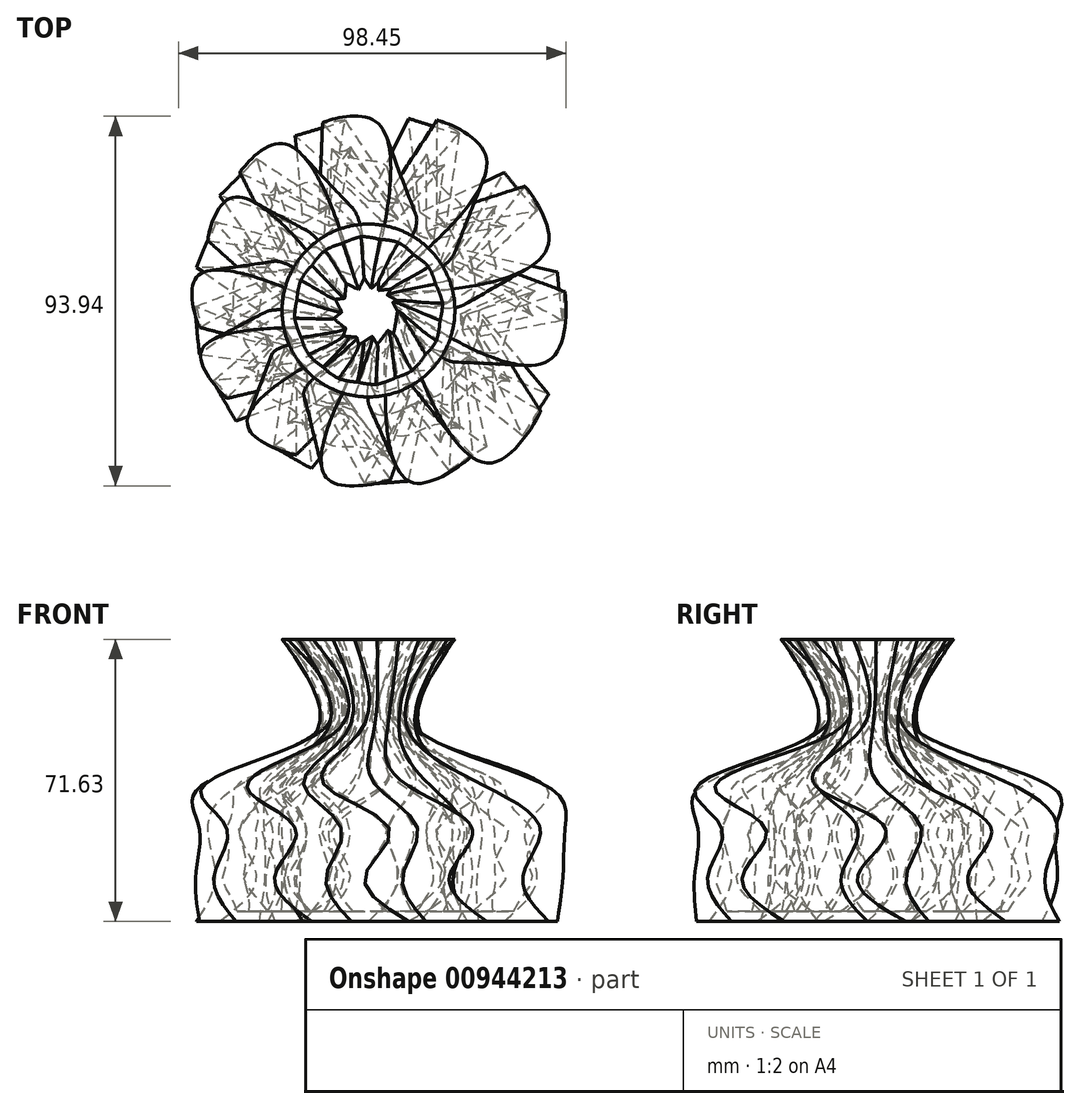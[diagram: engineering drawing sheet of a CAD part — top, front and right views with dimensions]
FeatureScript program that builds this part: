
annotation { "Feature Type Name" : "Feature", "Feature Type Description" : "" }
export const myFeature = defineFeature(function(context is Context, id is Id, definition is map)
    precondition{}
    {
        {
            var Q0;
            Q0=qCreatedBy(makeId("Top.planeOp"),FACE);
            var sketch = newSketch(context, id + "F0", { "sketchPlane" : qUnion([Q0])});
            skLineSegment(sketch, "E0", {"start": v(0, 27.93) * mm, "end": v(-18.62, 44.4) * mm});
            skLineSegment(sketch, "E1", {"start": v(-18.62, 44.4) * mm, "end": v(-16.65, 22.27) * mm});
            skLineSegment(sketch, "E2", {"start": v(-16.65, 22.27) * mm, "end": v(-37.8, 29.15) * mm});
            skLineSegment(sketch, "E3", {"start": v(-37.8, 29.15) * mm, "end": v(-25.5, 10.96) * mm});
            skLineSegment(sketch, "E4", {"start": v(-25.5, 10.96) * mm, "end": v(-43.7, 10.96) * mm});
            skLineSegment(sketch, "E5", {"start": v(-43.7, 10.96) * mm, "end": v(-27.71, 0) * mm});
            skLineSegment(sketch, "E6", {"start": v(-27.71, 0) * mm, "end": v(-42.95, -11.16) * mm});
            skLineSegment(sketch, "E7", {"start": v(-42.95, -11.16) * mm, "end": v(-23.78, -13.62) * mm});
            skLineSegment(sketch, "E8", {"start": v(-23.78, -13.62) * mm, "end": v(-33.61, -28.12) * mm});
            skLineSegment(sketch, "E9", {"start": v(-33.61, -28.12) * mm, "end": v(-16.65, -21.73) * mm});
            skLineSegment(sketch, "E10", {"start": v(-16.65, -21.73) * mm, "end": v(-14.44, -40.16) * mm});
            skLineSegment(sketch, "E11", {"start": v(-14.44, -40.16) * mm, "end": v(-4.36, -27.14) * mm});
            skLineSegment(sketch, "E12", {"start": v(-4.36, -27.14) * mm, "end": v(10.14, -43.36) * mm});
            skLineSegment(sketch, "E13", {"start": v(10.14, -43.36) * mm, "end": v(14.56, -22.71) * mm});
            skLineSegment(sketch, "E14", {"start": v(14.56, -22.71) * mm, "end": v(30.05, -34.5) * mm});
            skLineSegment(sketch, "E15", {"start": v(30.05, -34.5) * mm, "end": v(25.13, -12.39) * mm});
            skLineSegment(sketch, "E16", {"start": v(25.13, -12.39) * mm, "end": v(45.78, -21.24) * mm});
            skLineSegment(sketch, "E17", {"start": v(45.78, -21.24) * mm, "end": v(28.08, 0) * mm});
            skLineSegment(sketch, "E18", {"start": v(28.08, 0) * mm, "end": v(48, 9.74) * mm});
            skLineSegment(sketch, "E19", {"start": v(48, 9.74) * mm, "end": v(22.68, 15.64) * mm});
            skLineSegment(sketch, "E20", {"start": v(22.68, 15.64) * mm, "end": v(34.47, 35.05) * mm});
            skLineSegment(sketch, "E21", {"start": v(34.47, 35.05) * mm, "end": v(13.09, 24.98) * mm});
            skLineSegment(sketch, "E22", {"start": v(13.09, 24.98) * mm, "end": v(10.14, 48.82) * mm});
            skLineSegment(sketch, "E23", {"start": v(10.14, 48.82) * mm, "end": v(0, 27.93) * mm});
            skSolve(sketch);
        }
        {
            var Q0;
            Q0=qCreatedBy(makeId("Top.planeOp"),FACE);
            cPlane(context, id + "F1", {"entities" : qUnion([Q0]), "cplaneType" : CPlaneType.OFFSET, "offset" : 11.68 * mm, "width" : 152.4 * mm, "height" : 152.4 * mm});
        }
        {
            var Q0;
            Q0=qCreatedBy(makeId("Top.planeOp"),FACE);
            cPlane(context, id + "F2", {"entities" : qUnion([Q0]), "cplaneType" : CPlaneType.OFFSET, "offset" : 23.37 * mm, "width" : 152.4 * mm, "height" : 152.4 * mm});
        }
        {
            var Q0;
            Q0=qCreatedBy(makeId("Top.planeOp"),FACE);
            cPlane(context, id + "F3", {"entities" : qUnion([Q0]), "cplaneType" : CPlaneType.OFFSET, "offset" : 33.02 * mm, "width" : 152.4 * mm, "height" : 152.4 * mm});
        }
        {
            var Q0;
            Q0=qCreatedBy(makeId("Top.planeOp"),FACE);
            cPlane(context, id + "F4", {"entities" : qUnion([Q0]), "cplaneType" : CPlaneType.OFFSET, "offset" : 48 * mm, "width" : 152.4 * mm, "height" : 152.4 * mm});
        }
        {
            var Q0;
            Q0=qCreatedBy(makeId("Top.planeOp"),FACE);
            cPlane(context, id + "F5", {"entities" : qUnion([Q0]), "cplaneType" : CPlaneType.OFFSET, "offset" : 71.63 * mm, "width" : 152.4 * mm, "height" : 152.4 * mm});
        }
        {
            var Q0;
            Q0=qCreatedBy(id+"F1.planeOp",FACE);
            var sketch = newSketch(context, id + "F6", { "sketchPlane" : qUnion([Q0])});
            skLineSegment(sketch, "E24", {"start": v(7.76, 27.61) * mm, "end": v(-5.97, 48.34) * mm});
            skLineSegment(sketch, "E25", {"start": v(-5.97, 48.34) * mm, "end": v(-9.8, 26.46) * mm});
            skLineSegment(sketch, "E26", {"start": v(-9.8, 26.46) * mm, "end": v(-28.43, 38.58) * mm});
            skLineSegment(sketch, "E27", {"start": v(-28.43, 38.58) * mm, "end": v(-21.27, 17.83) * mm});
            skLineSegment(sketch, "E28", {"start": v(-21.27, 17.83) * mm, "end": v(-38.84, 22.54) * mm});
            skLineSegment(sketch, "E29", {"start": v(-38.84, 22.54) * mm, "end": v(-26.24, 7.81) * mm});
            skLineSegment(sketch, "E30", {"start": v(-26.24, 7.81) * mm, "end": v(-43.85, 0.98) * mm});
            skLineSegment(sketch, "E31", {"start": v(-43.85, 0.98) * mm, "end": v(-25.97, -6.36) * mm});
            skLineSegment(sketch, "E32", {"start": v(-25.97, -6.36) * mm, "end": v(-39.22, -17.82) * mm});
            skLineSegment(sketch, "E33", {"start": v(-39.22, -17.82) * mm, "end": v(-21.18, -16.04) * mm});
            skLineSegment(sketch, "E34", {"start": v(-21.18, -16.04) * mm, "end": v(-23.82, -34.42) * mm});
            skLineSegment(sketch, "E35", {"start": v(-23.82, -34.42) * mm, "end": v(-10.7, -24.44) * mm});
            skLineSegment(sketch, "E36", {"start": v(-10.7, -24.44) * mm, "end": v(-0.9, -43.87) * mm});
            skLineSegment(sketch, "E37", {"start": v(-0.9, -43.87) * mm, "end": v(8.72, -25.07) * mm});
            skLineSegment(sketch, "E38", {"start": v(8.72, -25.07) * mm, "end": v(20.62, -40.47) * mm});
            skLineSegment(sketch, "E39", {"start": v(20.62, -40.47) * mm, "end": v(21.6, -17.83) * mm});
            skLineSegment(sketch, "E40", {"start": v(21.6, -17.83) * mm, "end": v(39.25, -31.72) * mm});
            skLineSegment(sketch, "E41", {"start": v(39.25, -31.72) * mm, "end": v(27.66, -6.63) * mm});
            skLineSegment(sketch, "E42", {"start": v(27.66, -6.63) * mm, "end": v(49.4, -2.38) * mm});
            skLineSegment(sketch, "E43", {"start": v(49.4, -2.38) * mm, "end": v(26.48, 9.87) * mm});
            skLineSegment(sketch, "E44", {"start": v(26.48, 9.87) * mm, "end": v(42.9, 25.57) * mm});
            skLineSegment(sketch, "E45", {"start": v(42.9, 25.57) * mm, "end": v(19.64, 21.38) * mm});
            skLineSegment(sketch, "E46", {"start": v(19.64, 21.38) * mm, "end": v(22.96, 45.17) * mm});
            skLineSegment(sketch, "E47", {"start": v(22.96, 45.17) * mm, "end": v(7.76, 27.61) * mm});
            skLineSegment(sketch, "E48.0", {"start": v(-26.24, 7.81) * mm, "end": v(27.66, -6.63) * mm, "construction": true});
            skSolve(sketch);
        }
        {
            var Q0;
            Q0=qCreatedBy(id+"F2.planeOp",FACE);
            var sketch = newSketch(context, id + "F7", { "sketchPlane" : qUnion([Q0])});
            skLineSegment(sketch, "E49", {"start": v(4.71, 28.95) * mm, "end": v(-11.6, 47.7) * mm});
            skLineSegment(sketch, "E50", {"start": v(-11.6, 47.7) * mm, "end": v(-12.53, 25.52) * mm});
            skLineSegment(sketch, "E51", {"start": v(-12.53, 25.52) * mm, "end": v(-32.6, 35.1) * mm});
            skLineSegment(sketch, "E52", {"start": v(-32.6, 35.1) * mm, "end": v(-22.78, 15.46) * mm});
            skLineSegment(sketch, "E53", {"start": v(-22.78, 15.46) * mm, "end": v(-40.82, 17.84) * mm});
            skLineSegment(sketch, "E54", {"start": v(-40.82, 17.84) * mm, "end": v(-26.4, 4.88) * mm});
            skLineSegment(sketch, "E55", {"start": v(-26.4, 4.88) * mm, "end": v(-42.97, -4.2) * mm});
            skLineSegment(sketch, "E56", {"start": v(-42.97, -4.2) * mm, "end": v(-24.29, -9.13) * mm});
            skLineSegment(sketch, "E57", {"start": v(-24.29, -9.13) * mm, "end": v(-35.93, -22.23) * mm});
            skLineSegment(sketch, "E58", {"start": v(-35.93, -22.23) * mm, "end": v(-18.28, -18.1) * mm});
            skLineSegment(sketch, "E59", {"start": v(-18.28, -18.1) * mm, "end": v(-18.5, -36.67) * mm});
            skLineSegment(sketch, "E60", {"start": v(-18.5, -36.67) * mm, "end": v(-6.8, -25.07) * mm});
            skLineSegment(sketch, "E61", {"start": v(-6.8, -25.07) * mm, "end": v(5.46, -43.05) * mm});
            skLineSegment(sketch, "E62", {"start": v(5.46, -43.05) * mm, "end": v(12.54, -23.15) * mm});
            skLineSegment(sketch, "E63", {"start": v(12.54, -23.15) * mm, "end": v(26.36, -36.87) * mm});
            skLineSegment(sketch, "E64", {"start": v(26.36, -36.87) * mm, "end": v(24.37, -14.3) * mm});
            skLineSegment(sketch, "E65", {"start": v(24.37, -14.3) * mm, "end": v(43.69, -25.77) * mm});
            skLineSegment(sketch, "E66", {"start": v(43.69, -25.77) * mm, "end": v(28.91, -2.4) * mm});
            skLineSegment(sketch, "E67", {"start": v(28.91, -2.4) * mm, "end": v(49.92, 4.65) * mm});
            skLineSegment(sketch, "E68", {"start": v(49.92, 4.65) * mm, "end": v(25.6, 13.8) * mm});
            skLineSegment(sketch, "E69", {"start": v(25.6, 13.8) * mm, "end": v(39.82, 31.52) * mm});
            skLineSegment(sketch, "E70", {"start": v(39.82, 31.52) * mm, "end": v(17.3, 24.32) * mm});
            skLineSegment(sketch, "E71", {"start": v(17.3, 24.32) * mm, "end": v(17.5, 48.34) * mm});
            skLineSegment(sketch, "E72", {"start": v(17.5, 48.34) * mm, "end": v(4.71, 28.95) * mm});
            skLineSegment(sketch, "E73.0", {"start": v(-26.4, 4.88) * mm, "end": v(28.91, -2.4) * mm, "construction": true});
            skSolve(sketch);
        }
        {
            var Q0;
            Q0=qCreatedBy(id+"F3.planeOp",FACE);
            var sketch = newSketch(context, id + "F8", { "sketchPlane" : qUnion([Q0])});
            skLineSegment(sketch, "E74", {"start": v(11.5, 25.38) * mm, "end": v(1.6, 48.18) * mm});
            skLineSegment(sketch, "E75", {"start": v(1.6, 48.18) * mm, "end": v(-5.97, 27.3) * mm});
            skLineSegment(sketch, "E76", {"start": v(-5.97, 27.3) * mm, "end": v(-22.22, 42.47) * mm});
            skLineSegment(sketch, "E77", {"start": v(-22.22, 42.47) * mm, "end": v(-18.77, 20.79) * mm});
            skLineSegment(sketch, "E78", {"start": v(-18.77, 20.79) * mm, "end": v(-35.26, 28.47) * mm});
            skLineSegment(sketch, "E79", {"start": v(-35.26, 28.47) * mm, "end": v(-25.41, 11.78) * mm});
            skLineSegment(sketch, "E80", {"start": v(-25.41, 11.78) * mm, "end": v(-43.94, 8.11) * mm});
            skLineSegment(sketch, "E81", {"start": v(-43.94, 8.11) * mm, "end": v(-27.6, -2.22) * mm});
            skLineSegment(sketch, "E82", {"start": v(-27.6, -2.22) * mm, "end": v(-42.64, -11.2) * mm});
            skLineSegment(sketch, "E83", {"start": v(-42.64, -11.2) * mm, "end": v(-24.57, -12.58) * mm});
            skLineSegment(sketch, "E84", {"start": v(-24.57, -12.58) * mm, "end": v(-30.35, -30.23) * mm});
            skLineSegment(sketch, "E85", {"start": v(-30.35, -30.23) * mm, "end": v(-15.71, -22.68) * mm});
            skLineSegment(sketch, "E86", {"start": v(-15.71, -22.68) * mm, "end": v(-9.43, -43.5) * mm});
            skLineSegment(sketch, "E87", {"start": v(-9.43, -43.5) * mm, "end": v(3.3, -26.67) * mm});
            skLineSegment(sketch, "E88", {"start": v(3.3, -26.67) * mm, "end": v(12.36, -43.9) * mm});
            skLineSegment(sketch, "E89", {"start": v(12.36, -43.9) * mm, "end": v(17.25, -21.78) * mm});
            skLineSegment(sketch, "E90", {"start": v(17.25, -21.78) * mm, "end": v(32.23, -38.52) * mm});
            skLineSegment(sketch, "E91", {"start": v(32.23, -38.52) * mm, "end": v(25.16, -11.8) * mm});
            skLineSegment(sketch, "E92", {"start": v(25.16, -11.8) * mm, "end": v(47.32, -11.39) * mm});
            skLineSegment(sketch, "E93", {"start": v(47.32, -11.39) * mm, "end": v(26.87, 4.66) * mm});
            skLineSegment(sketch, "E94", {"start": v(26.87, 4.66) * mm, "end": v(45.77, 17.27) * mm});
            skLineSegment(sketch, "E95", {"start": v(45.77, 17.27) * mm, "end": v(22.13, 17.18) * mm});
            skLineSegment(sketch, "E96", {"start": v(22.13, 17.18) * mm, "end": v(29.53, 40.03) * mm});
            skLineSegment(sketch, "E97", {"start": v(29.53, 40.03) * mm, "end": v(11.5, 25.38) * mm});
            skLineSegment(sketch, "E98.0", {"start": v(-25.41, 11.78) * mm, "end": v(25.16, -11.8) * mm, "construction": true});
            skSolve(sketch);
        }
        {
            var Q0;
            Q0=qCreatedBy(id+"F4.planeOp",FACE);
            var sketch = newSketch(context, id + "F9", { "sketchPlane" : qUnion([Q0])});
            skCircle(sketch, "E99", {"center": v(0, 0) * mm, "radius": 13.38 * mm});
            skSolve(sketch);
        }
        {
            var Q0;
            Q0=qCreatedBy(id+"F5.planeOp",FACE);
            var sketch = newSketch(context, id + "F10", { "sketchPlane" : qUnion([Q0])});
            skCircle(sketch, "E100", {"center": v(0, 0) * mm, "radius": 21.95 * mm});
            skSolve(sketch);
        }
        {
            var Q0;
            Q0=makeQuery(id+"F0.imprint","IMPRINT",FACE,{"disambiguationData":[TD([[makeQuery(id+"F0.imprint","IMPRINT",EDGE,{"derivedFrom":sQuery(id+"F0.wireOp",EDGE,"E0")}),1.0]])]});
            var Q1;
            Q1=makeQuery(id+"F6.imprint","IMPRINT",FACE,{"disambiguationData":[TD([[makeQuery(id+"F6.imprint","IMPRINT",EDGE,{"derivedFrom":sQuery(id+"F6.wireOp",EDGE,"E24")}),1.0]])]});
            var Q2;
            Q2=makeQuery(id+"F7.imprint","IMPRINT",FACE,{"disambiguationData":[TD([[makeQuery(id+"F7.imprint","IMPRINT",EDGE,{"derivedFrom":sQuery(id+"F7.wireOp",EDGE,"E49")}),1.0]])]});
            var Q3;
            Q3=makeQuery(id+"F8.imprint","IMPRINT",FACE,{"disambiguationData":[TD([[makeQuery(id+"F8.imprint","IMPRINT",EDGE,{"derivedFrom":sQuery(id+"F8.wireOp",EDGE,"E74")}),1.0]])]});
            var Q4;
            Q4=makeQuery(id+"F9.imprint","IMPRINT",FACE,{"disambiguationData":[TD([[makeQuery(id+"F9.imprint","IMPRINT",EDGE,{"derivedFrom":sQuery(id+"F9.wireOp",EDGE,"E99")}),1.0]])]});
            var Q5;
            Q5=makeQuery(id+"F10.imprint","IMPRINT",FACE,{"disambiguationData":[TD([[makeQuery(id+"F10.imprint","IMPRINT",EDGE,{"derivedFrom":sQuery(id+"F10.wireOp",EDGE,"E100")}),1.0]])]});
            loft(context, id + "F11", {"sheetProfilesArray" : [{ "sheetProfileEntities" : qUnion([Q0]) }, { "sheetProfileEntities" : qUnion([Q1]) }, { "sheetProfileEntities" : qUnion([Q2]) }, { "sheetProfileEntities" : qUnion([Q3]) }, { "sheetProfileEntities" : qUnion([Q4]) }, { "sheetProfileEntities" : qUnion([Q5]) }]});
        }
        {
            var Q0;
            Q0=makeQuery(id+"F11.opLoft","CAP_FACE",FACE,{"disambiguationData":[OSD([makeQuery(id+"F10.imprint","IMPRINT",FACE,{"disambiguationData":[TD([[makeQuery(id+"F10.imprint","IMPRINT",EDGE,{"derivedFrom":sQuery(id+"F10.wireOp",EDGE,"E100")}),1.0]])]})])],"isStart":true});
            shell(context, id + "F12", {"entities" : qUnion([Q0]), "thickness" : 2.54 * mm});
        }
    });
